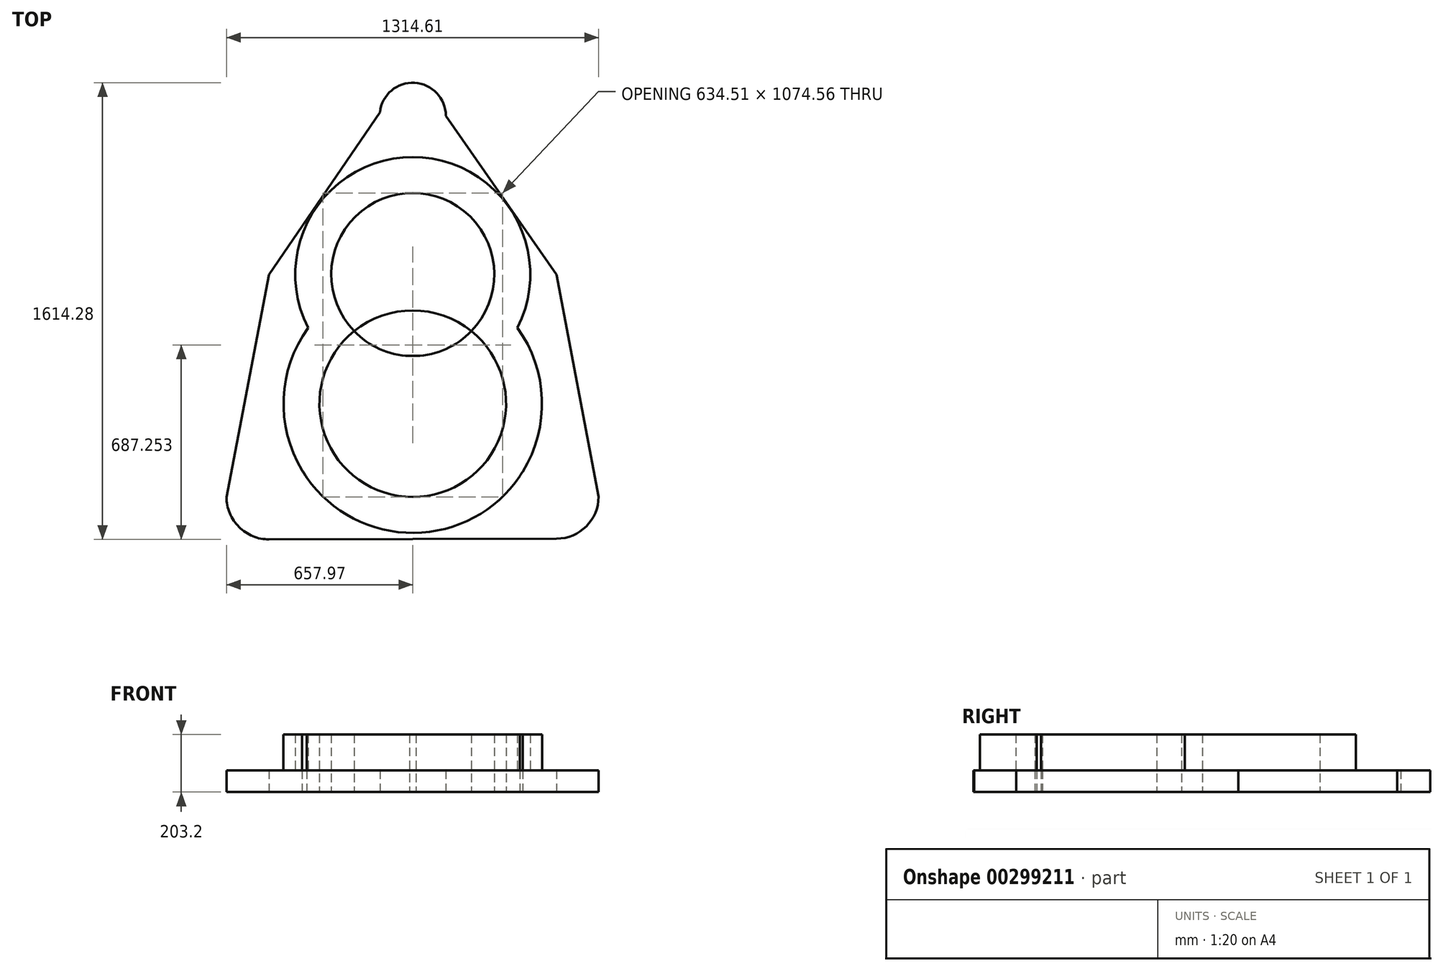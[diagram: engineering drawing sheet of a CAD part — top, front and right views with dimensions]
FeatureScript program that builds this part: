
annotation { "Feature Type Name" : "Feature", "Feature Type Description" : "" }
export const myFeature = defineFeature(function(context is Context, id is Id, definition is map)
    precondition{}
    {
        {
            var Q0;
            Q0=qCreatedBy(makeId("Top.planeOp"),FACE);
            var sketch = newSketch(context, id + "F0", { "sketchPlane" : qUnion([Q0])});
            skCircle(sketch, "E0", {"center": v(0, 0) * mm, "radius": 456.72 * mm});
            skCircle(sketch, "E1", {"center": v(0, 0) * mm, "radius": 329.72 * mm});
            skCircle(sketch, "E2", {"center": v(0, 456.72) * mm, "radius": 288.13 * mm});
            skArc(sketch, "E3", {"start": v(369.78, 268.05) * mm, "mid": v(0, 871.84) * mm, "end": v(-369.78, 268.05) * mm});
            skCircle(sketch, "E4", {"center": v(0, 1017.73) * mm, "radius": 116.86 * mm});
            skLineSegment(sketch, "E5", {"start": v(-116.1, 1030.96) * mm, "end": v(-508, 456.72) * mm});
            skCircle(sketch, "E6", {"center": v(0, 0) * mm, "radius": 169.16 * mm});
            skCircle(sketch, "E7", {"center": v(508, -328.54) * mm, "radius": 148.64 * mm});
            skCircle(sketch, "E8", {"center": v(-508, -329.72) * mm, "radius": 149.97 * mm});
            skLineSegment(sketch, "E9", {"start": v(-116.1, 1030.96) * mm, "end": v(-136.87, 848.63) * mm});
            skLineSegment(sketch, "E10", {"start": v(508, 456.72) * mm, "end": v(656.64, -328.54) * mm});
            skLineSegment(sketch, "E11", {"start": v(-657.97, -329.72) * mm, "end": v(-508, 456.72) * mm});
            skLineSegment(sketch, "E12", {"start": v(508, -477.18) * mm, "end": v(-508, -479.69) * mm});
            skLineSegment(sketch, "E13", {"start": v(-508, -179.74) * mm, "end": v(-419.86, -179.74) * mm});
            skLineSegment(sketch, "E14", {"start": v(508, -179.9) * mm, "end": v(419.8, -179.9) * mm});
            skLineSegment(sketch, "E15", {"start": v(116.86, 1017.73) * mm, "end": v(140.47, 847.36) * mm});
            skLineSegment(sketch, "E16", {"start": v(116.86, 1017.73) * mm, "end": v(508, 456.72) * mm});
            skSolve(sketch);
        }
        {
            var Q0;
            {var subQ0=sQuery(id+"F0.wireOp",EDGE,"E3");var subQ1=sQuery(id+"F0.wireOp",EDGE,"E0");var subQ2=makeQuery(id+"F0.imprint","INTERSECT",VERTEX,{"disambiguationData":[OD(0.0)],"derivedFrom":[subQ1,subQ0]});Q0=makeQuery(id+"F0.imprint","IMPRINT",FACE,{"disambiguationData":[TD([[makeQuery(id+"F0.imprint","IMPRINT",EDGE,{"disambiguationData":[TD([[subQ2,-1.0]])],"derivedFrom":subQ1}),-1.0]])]});}
            var Q1;
            {var subQ1=sQuery(id+"F0.wireOp",EDGE,"E0");var subQ7=sQuery(id+"F0.wireOp",EDGE,"E3");var subQ8=makeQuery(id+"F0.imprint","INTERSECT",VERTEX,{"disambiguationData":[OD(0.0)],"derivedFrom":[subQ1,subQ7]});Q1=makeQuery(id+"F0.imprint","IMPRINT",FACE,{"disambiguationData":[TD([[makeQuery(id+"F0.imprint","IMPRINT",EDGE,{"disambiguationData":[TD([[subQ8,-1.0]])],"derivedFrom":subQ1}),1.0]])]});}
            var Q2;
            {var subQ0=sQuery(id+"F0.wireOp",EDGE,"E2");var subQ1=sQuery(id+"F0.wireOp",EDGE,"E1");var subQ2=makeQuery(id+"F0.imprint","INTERSECT",VERTEX,{"disambiguationData":[OD(0.0)],"derivedFrom":[subQ1,subQ0]});Q2=makeQuery(id+"F0.imprint","IMPRINT",FACE,{"disambiguationData":[TD([[makeQuery(id+"F0.imprint","IMPRINT",EDGE,{"disambiguationData":[TD([[subQ2,1.0]])],"derivedFrom":subQ1}),1.0]])]});}
            extrude(context, id + "F1", {"entities" : qUnion([Q0, Q1, Q2]), "depth" : 203.2 * mm});
        }
        {
            var Q0;
            {var subQ0=sQuery(id+"F0.wireOp",EDGE,"E9");Q0=makeQuery(id+"F0.imprint","IMPRINT",FACE,{"disambiguationData":[TD([[makeQuery(id+"F0.imprint","IMPRINT",EDGE,{"derivedFrom":subQ0}),1.0]])]});}
            var Q1;
            {var subQ4=sQuery(id+"F0.wireOp",EDGE,"E5");Q1=makeQuery(id+"F0.imprint","IMPRINT",FACE,{"disambiguationData":[TD([[makeQuery(id+"F0.imprint","IMPRINT",EDGE,{"derivedFrom":subQ4}),1.0]])]});}
            var Q2;
            {var subQ0=sQuery(id+"F0.wireOp",EDGE,"E14");Q2=makeQuery(id+"F0.imprint","IMPRINT",FACE,{"disambiguationData":[TD([[makeQuery(id+"F0.imprint","IMPRINT",EDGE,{"derivedFrom":subQ0}),-1.0]])]});}
            var Q3;
            {var subQ0=sQuery(id+"F0.wireOp",EDGE,"E14");Q3=makeQuery(id+"F0.imprint","IMPRINT",FACE,{"disambiguationData":[TD([[makeQuery(id+"F0.imprint","IMPRINT",EDGE,{"derivedFrom":subQ0}),1.0]])]});}
            var Q4;
            {var subQ0=sQuery(id+"F0.wireOp",EDGE,"E8");var subQ1=sQuery(id+"F0.wireOp",EDGE,"E0");var subQ2=makeQuery(id+"F0.imprint","INTERSECT",VERTEX,{"disambiguationData":[OD(1.0)],"derivedFrom":[subQ1,subQ0]});Q4=makeQuery(id+"F0.imprint","IMPRINT",FACE,{"disambiguationData":[TD([[makeQuery(id+"F0.imprint","IMPRINT",EDGE,{"disambiguationData":[TD([[subQ2,-1.0]])],"derivedFrom":subQ1}),-1.0]])]});}
            var Q5;
            {var subQ0=sQuery(id+"F0.wireOp",EDGE,"E13");Q5=makeQuery(id+"F0.imprint","IMPRINT",FACE,{"disambiguationData":[TD([[makeQuery(id+"F0.imprint","IMPRINT",EDGE,{"derivedFrom":subQ0}),-1.0]])]});}
            extrude(context, id + "F2", {"entities" : qUnion([Q0, Q1, Q2, Q3, Q4, Q5]), "operationType" : NewBodyOperationType.ADD, "depth" : 76.2 * mm});
        }
        {
            var Q0;
            {var subQ0=sQuery(id+"F0.wireOp",EDGE,"E7");var subQ2=sQuery(id+"F0.wireOp",EDGE,"E0");var subQ3=makeQuery(id+"F0.imprint","INTERSECT",VERTEX,{"disambiguationData":[OD(0.0)],"derivedFrom":[subQ2,subQ0]});Q0=makeQuery(id+"F0.imprint","IMPRINT",FACE,{"disambiguationData":[TD([[makeQuery(id+"F0.imprint","IMPRINT",EDGE,{"disambiguationData":[TD([[subQ3,-1.0]])],"derivedFrom":subQ2}),-1.0]])]});}
            var Q1;
            {var subQ1=sQuery(id+"F0.wireOp",EDGE,"E8");var subQ6=sQuery(id+"F0.wireOp",EDGE,"E0");var subQ7=makeQuery(id+"F0.imprint","INTERSECT",VERTEX,{"disambiguationData":[OD(0.0)],"derivedFrom":[subQ6,subQ1]});Q1=makeQuery(id+"F0.imprint","IMPRINT",FACE,{"disambiguationData":[TD([[makeQuery(id+"F0.imprint","IMPRINT",EDGE,{"disambiguationData":[TD([[subQ7,-1.0]])],"derivedFrom":subQ6}),-1.0]])]});}
            var Q2;
            {var subQ0=sQuery(id+"F0.wireOp",EDGE,"E4");var subQ1=makeQuery(id+"F0.imprint","INTERSECT",VERTEX,{"derivedFrom":[subQ0,sQuery(id+"F0.wireOp",EDGE,"E5"),sQuery(id+"F0.wireOp",EDGE,"E9")]});Q2=makeQuery(id+"F0.imprint","IMPRINT",FACE,{"disambiguationData":[TD([[makeQuery(id+"F0.imprint","IMPRINT",EDGE,{"disambiguationData":[TD([[subQ1,1.0]])],"derivedFrom":subQ0}),1.0]])]});}
            extrude(context, id + "F3", {"entities" : qUnion([Q0, Q1, Q2]), "operationType" : NewBodyOperationType.ADD, "depth" : 76.2 * mm});
        }
    });
